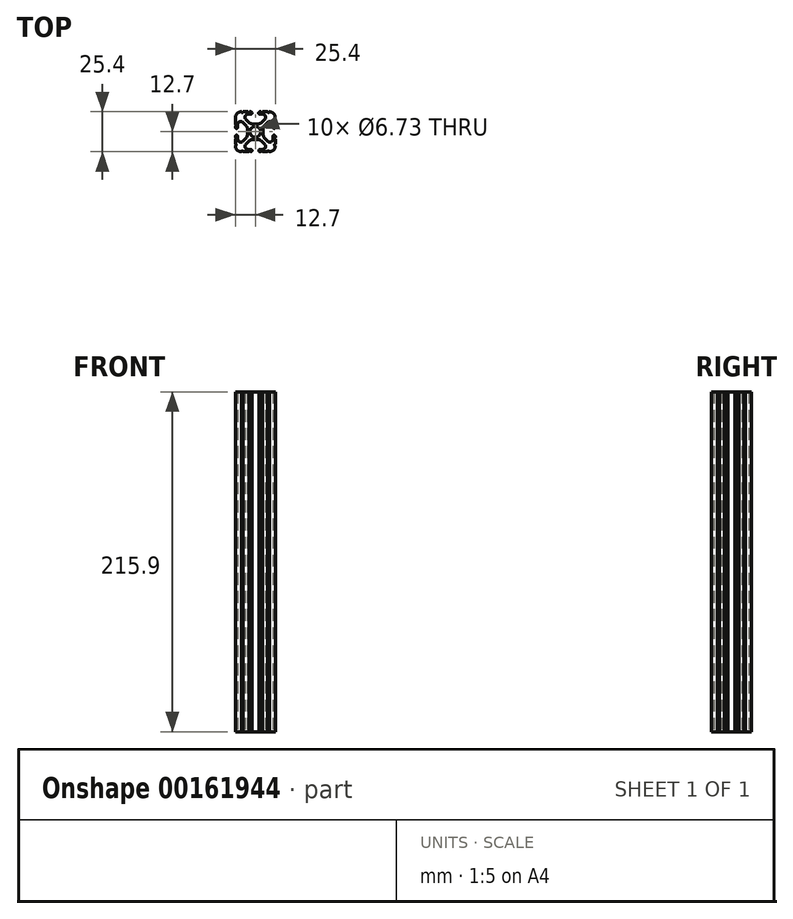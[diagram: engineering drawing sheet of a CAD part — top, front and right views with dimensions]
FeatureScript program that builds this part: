
annotation { "Feature Type Name" : "Feature", "Feature Type Description" : "" }
export const myFeature = defineFeature(function(context is Context, id is Id, definition is map)
    precondition{}
    {
        {
            var Q0;
            Q0=qCreatedBy(makeId("Top.planeOp"),FACE);
            var sketch = newSketch(context, id + "F0", { "sketchPlane" : qUnion([Q0])});
            skCircle(sketch, "E0", {"center": v(-12.7, 12.7) * mm, "radius": 3.36 * mm});
            skLineSegment(sketch, "E1.bottom", {"start": v(-11.24, 17.64) * mm, "end": v(-14.16, 17.64) * mm});
            skLineSegment(sketch, "E1.top", {"start": v(-11.24, 7.76) * mm, "end": v(-14.16, 7.76) * mm});
            skLineSegment(sketch, "E1.left", {"start": v(-7.76, 14.16) * mm, "end": v(-7.76, 11.24) * mm});
            skLineSegment(sketch, "E1.right", {"start": v(-17.64, 14.16) * mm, "end": v(-17.64, 11.24) * mm});
            skPoint(sketch, "E2.visualSharp", {"position": v(-25.4, 25.4) * mm});
            skPoint(sketch, "E3.visualSharp", {"position": v(0, 25.4) * mm});
            skPoint(sketch, "E4.visualSharp", {"position": v(0, 0) * mm});
            skPoint(sketch, "E5.visualSharp", {"position": v(-25.4, 0) * mm});
            skLineSegment(sketch, "E6.0", {"start": v(-18.7, 20.6) * mm, "end": v(-16.85, 18.76) * mm});
            skLineSegment(sketch, "E7.0", {"start": v(-20.6, 18.7) * mm, "end": v(-18.76, 16.85) * mm});
            skPoint(sketch, "E8.orphan", {"position": v(-23.85, 1.55) * mm});
            skPoint(sketch, "E9.orphan", {"position": v(-23.85, 23.85) * mm});
            skPoint(sketch, "E10.orphan", {"position": v(-1.55, 23.85) * mm});
            skPoint(sketch, "E11.orphan", {"position": v(-1.55, 1.55) * mm});
            skLineSegment(sketch, "E12", {"start": v(-8.55, 6.64) * mm, "end": v(-6.7, 4.8) * mm});
            skLineSegment(sketch, "E13.0", {"start": v(-18.7, 4.8) * mm, "end": v(-16.85, 6.64) * mm});
            skLineSegment(sketch, "E14.0", {"start": v(-20.6, 6.7) * mm, "end": v(-18.76, 8.55) * mm});
            skLineSegment(sketch, "E15.0", {"start": v(-8.55, 18.76) * mm, "end": v(-6.7, 20.6) * mm});
            skPoint(sketch, "E16.visualSharp", {"position": v(-23.85, 21.95) * mm});
            skArc(sketch, "E16.filletArc", {"start": v(-20.6, 18.7) * mm, "mid": v(-22.68, 19.1) * mm, "end": v(-23.85, 17.35) * mm});
            skPoint(sketch, "E17.visualSharp", {"position": v(-21.95, 23.85) * mm});
            skArc(sketch, "E17.filletArc", {"start": v(-17.35, 23.85) * mm, "mid": v(-19.1, 22.68) * mm, "end": v(-18.7, 20.6) * mm});
            skPoint(sketch, "E18.visualSharp", {"position": v(-5.34, 23.85) * mm});
            skLineSegment(sketch, "E19", {"start": v(-17.35, 23.85) * mm, "end": v(-15.58, 23.85) * mm});
            skLineSegment(sketch, "E20", {"start": v(-23.85, 17.35) * mm, "end": v(-23.85, 15.62) * mm});
            skLineSegment(sketch, "E21", {"start": v(-8.05, 1.55) * mm, "end": v(-9.78, 1.55) * mm});
            skArc(sketch, "E22.filletArc", {"start": v(-6.7, 20.6) * mm, "mid": v(-6.3, 22.68) * mm, "end": v(-8.05, 23.85) * mm});
            skPoint(sketch, "E23.visualSharp", {"position": v(-1.55, 3.45) * mm});
            skPoint(sketch, "E24.visualSharp", {"position": v(-3.45, 1.55) * mm});
            skArc(sketch, "E24.filletArc", {"start": v(-8.05, 1.55) * mm, "mid": v(-6.3, 2.73) * mm, "end": v(-6.7, 4.8) * mm});
            skArc(sketch, "E25.filletArc", {"start": v(-18.7, 4.8) * mm, "mid": v(-19.1, 2.73) * mm, "end": v(-17.35, 1.55) * mm});
            skArc(sketch, "E26.filletArc", {"start": v(-23.85, 8.05) * mm, "mid": v(-22.68, 6.3) * mm, "end": v(-20.6, 6.7) * mm});
            skLineSegment(sketch, "E27.bottom", {"start": v(-4.9, 0) * mm, "end": v(-8.05, 0) * mm});
            skLineSegment(sketch, "E27.top", {"start": v(-4.92, 25.4) * mm, "end": v(-8.05, 25.4) * mm});
            skLineSegment(sketch, "E27.left", {"start": v(0, 4.9) * mm, "end": v(0, 8.05) * mm});
            skLineSegment(sketch, "E27.right", {"start": v(-25.4, 4.9) * mm, "end": v(-25.4, 8.05) * mm});
            skArc(sketch, "E28.filletArc", {"start": v(-25.4, 3.81) * mm, "mid": v(-24.28, 1.12) * mm, "end": v(-21.59, 0) * mm});
            skArc(sketch, "E29.filletArc", {"start": v(-3.81, 0) * mm, "mid": v(-1.12, 1.12) * mm, "end": v(0, 3.8) * mm});
            skArc(sketch, "E30.filletArc", {"start": v(0, 21.59) * mm, "mid": v(-1.12, 24.28) * mm, "end": v(-3.8, 25.4) * mm});
            skArc(sketch, "E31.filletArc", {"start": v(-21.59, 25.4) * mm, "mid": v(-24.28, 24.28) * mm, "end": v(-25.4, 21.59) * mm});
            skPoint(sketch, "E32.newPointA", {"position": v(-17.64, 7.76) * mm});
            skArc(sketch, "E32.filletArc", {"start": v(-14.16, 7.76) * mm, "mid": v(-15.62, 7.47) * mm, "end": v(-16.85, 6.64) * mm});
            skPoint(sketch, "E33.newPointA", {"position": v(-7.76, 7.76) * mm});
            skArc(sketch, "E33.filletArc", {"start": v(-8.55, 6.64) * mm, "mid": v(-9.78, 7.47) * mm, "end": v(-11.24, 7.76) * mm});
            skArc(sketch, "E34.filletArc", {"start": v(-7.76, 11.24) * mm, "mid": v(-7.47, 9.78) * mm, "end": v(-6.64, 8.55) * mm});
            skArc(sketch, "E35.filletArc", {"start": v(-6.64, 16.85) * mm, "mid": v(-7.47, 15.62) * mm, "end": v(-7.76, 14.16) * mm});
            skPoint(sketch, "E36.newPointB", {"position": v(-7.76, 17.64) * mm});
            skArc(sketch, "E36.filletArc", {"start": v(-11.24, 17.64) * mm, "mid": v(-9.78, 17.93) * mm, "end": v(-8.55, 18.76) * mm});
            skPoint(sketch, "E37.newPointB", {"position": v(-17.64, 17.64) * mm});
            skArc(sketch, "E37.filletArc", {"start": v(-16.85, 18.76) * mm, "mid": v(-15.62, 17.93) * mm, "end": v(-14.16, 17.64) * mm});
            skArc(sketch, "E38.filletArc", {"start": v(-17.64, 14.16) * mm, "mid": v(-17.93, 15.62) * mm, "end": v(-18.76, 16.85) * mm});
            skArc(sketch, "E39.filletArc", {"start": v(-18.76, 8.55) * mm, "mid": v(-17.93, 9.78) * mm, "end": v(-17.64, 11.24) * mm});
            skLineSegment(sketch, "E40", {"start": v(-6.64, 8.55) * mm, "end": v(-4.8, 6.7) * mm});
            skPoint(sketch, "E41.visualSharp", {"position": v(-1.55, 21.95) * mm});
            skArc(sketch, "E42.filletArc", {"start": v(-4.8, 6.7) * mm, "mid": v(-2.73, 6.3) * mm, "end": v(-1.55, 8.05) * mm});
            skLineSegment(sketch, "E43", {"start": v(-1.55, 8.05) * mm, "end": v(-1.55, 9.78) * mm});
            skLineSegment(sketch, "E44", {"start": v(-6.64, 16.85) * mm, "end": v(-4.8, 18.7) * mm});
            skArc(sketch, "E45.filletArc", {"start": v(-1.55, 17.35) * mm, "mid": v(-2.73, 19.1) * mm, "end": v(-4.8, 18.7) * mm});
            skArc(sketch, "E46", {"start": v(-23.85, 9.78) * mm, "mid": v(-24.63, 10.56) * mm, "end": v(-25.4, 9.78) * mm});
            skArc(sketch, "E47", {"start": v(-25.4, 15.62) * mm, "mid": v(-24.63, 14.86) * mm, "end": v(-23.85, 15.62) * mm});
            skArc(sketch, "E48", {"start": v(-15.62, 23.85) * mm, "mid": v(-14.83, 24.63) * mm, "end": v(-15.62, 25.4) * mm});
            skArc(sketch, "E49", {"start": v(-9.78, 25.4) * mm, "mid": v(-10.6, 24.63) * mm, "end": v(-9.78, 23.85) * mm});
            skArc(sketch, "E50", {"start": v(-1.55, 15.62) * mm, "mid": v(-0.77, 14.88) * mm, "end": v(0, 15.62) * mm});
            skArc(sketch, "E51", {"start": v(0, 9.78) * mm, "mid": v(-0.77, 10.5) * mm, "end": v(-1.55, 9.78) * mm});
            skArc(sketch, "E52", {"start": v(-9.78, 1.55) * mm, "mid": v(-10.4, 0.77) * mm, "end": v(-9.78, 0) * mm});
            skArc(sketch, "E53", {"start": v(-15.62, 0) * mm, "mid": v(-14.85, 0.77) * mm, "end": v(-15.62, 1.55) * mm});
            skLineSegment(sketch, "E54.trimOffspring", {"start": v(-15.62, 1.55) * mm, "end": v(-17.35, 1.55) * mm});
            skLineSegment(sketch, "E55.trimOffspring", {"start": v(-16.7, 0) * mm, "end": v(-20.5, 0) * mm});
            skLineSegment(sketch, "E56.trimOffspring", {"start": v(-1.55, 15.62) * mm, "end": v(-1.55, 17.35) * mm});
            skLineSegment(sketch, "E57.trimOffspring", {"start": v(0, 15.62) * mm, "end": v(0, 16.26) * mm});
            skLineSegment(sketch, "E58.trimOffspring", {"start": v(-23.85, 9.78) * mm, "end": v(-23.85, 8.05) * mm});
            skLineSegment(sketch, "E59.trimOffspring", {"start": v(-25.4, 15.62) * mm, "end": v(-25.4, 16.26) * mm});
            skLineSegment(sketch, "E60.trimOffspring", {"start": v(-9.86, 23.85) * mm, "end": v(-8.05, 23.85) * mm});
            skLineSegment(sketch, "E61.trimOffspring", {"start": v(-15.58, 25.4) * mm, "end": v(-16.25, 25.4) * mm});
            skPoint(sketch, "E62.start.orphan", {"position": v(-15.62, 17.93) * mm});
            skPoint(sketch, "E63.start.orphan", {"position": v(-9.78, 17.93) * mm});
            skPoint(sketch, "E64.start.orphan", {"position": v(-7.47, 15.62) * mm});
            skPoint(sketch, "E65.start.orphan", {"position": v(-7.47, 9.78) * mm});
            skPoint(sketch, "E66.start.orphan", {"position": v(-17.93, 15.62) * mm});
            skPoint(sketch, "E67.start.orphan", {"position": v(-17.93, 9.78) * mm});
            skPoint(sketch, "E68.start.orphan", {"position": v(-9.78, 7.47) * mm});
            skPoint(sketch, "E69.start.orphan", {"position": v(-15.62, 7.47) * mm});
            skPoint(sketch, "E70.endSnap0", {"position": v(0, 18.6) * mm});
            skPoint(sketch, "E71.startSnap0", {"position": v(-1.55, 8.92) * mm});
            skArc(sketch, "E72", {"start": v(-4.92, 25.4) * mm, "mid": v(-4.37, 24.9) * mm, "end": v(-3.81, 25.4) * mm});
            skArc(sketch, "E73", {"start": v(-9.14, 25.4) * mm, "mid": v(-8.6, 24.86) * mm, "end": v(-8.05, 25.4) * mm});
            skArc(sketch, "E74", {"start": v(-17.35, 25.4) * mm, "mid": v(-16.8, 24.86) * mm, "end": v(-16.25, 25.4) * mm});
            skArc(sketch, "E75", {"start": v(-21.59, 25.4) * mm, "mid": v(-21.04, 24.85) * mm, "end": v(-20.49, 25.4) * mm});
            skLineSegment(sketch, "E76", {"start": v(-25.4, 21.59) * mm, "end": v(-25.4, 20.5) * mm});
            skArc(sketch, "E77", {"start": v(-25.4, 16.26) * mm, "mid": v(-24.84, 16.8) * mm, "end": v(-25.4, 17.35) * mm});
            skArc(sketch, "E78", {"start": v(-25.4, 8.05) * mm, "mid": v(-24.9, 8.6) * mm, "end": v(-25.4, 9.15) * mm});
            skArc(sketch, "E79", {"start": v(-25.4, 3.81) * mm, "mid": v(-24.85, 4.36) * mm, "end": v(-25.4, 4.9) * mm});
            skArc(sketch, "E80", {"start": v(-20.5, 0) * mm, "mid": v(-21.04, 0.55) * mm, "end": v(-21.59, 0) * mm});
            skArc(sketch, "E81", {"start": v(-15.62, 0) * mm, "mid": v(-16.16, 0.54) * mm, "end": v(-16.7, 0) * mm});
            skArc(sketch, "E82", {"start": v(-8.05, 0) * mm, "mid": v(-8.6, 0.55) * mm, "end": v(-9.15, 0) * mm});
            skArc(sketch, "E83", {"start": v(-3.81, 0) * mm, "mid": v(-4.35, 0.54) * mm, "end": v(-4.9, 0) * mm});
            skLineSegment(sketch, "E84.trimOffspring", {"start": v(-17.35, 25.4) * mm, "end": v(-20.49, 25.4) * mm});
            skLineSegment(sketch, "E85.trimOffspring", {"start": v(-25.4, 17.35) * mm, "end": v(-25.4, 21.59) * mm});
            skLineSegment(sketch, "E86.trimOffspring", {"start": v(-25.4, 9.15) * mm, "end": v(-25.4, 9.78) * mm});
            skLineSegment(sketch, "E87.trimOffspring", {"start": v(-9.15, 0) * mm, "end": v(-9.78, 0) * mm});
            skArc(sketch, "E88", {"start": v(0, 4.9) * mm, "mid": v(-0.54, 4.36) * mm, "end": v(0, 3.8) * mm});
            skArc(sketch, "E89", {"start": v(0, 9.15) * mm, "mid": v(-0.54, 8.6) * mm, "end": v(0, 8.05) * mm});
            skLineSegment(sketch, "E90.trimOffspring", {"start": v(0, 9.15) * mm, "end": v(0, 9.78) * mm});
            skArc(sketch, "E91", {"start": v(0, 21.59) * mm, "mid": v(-0.55, 21.04) * mm, "end": v(0, 20.5) * mm});
            skArc(sketch, "E92", {"start": v(0, 17.35) * mm, "mid": v(-0.55, 16.8) * mm, "end": v(0, 16.26) * mm});
            skLineSegment(sketch, "E93.trimOffspring", {"start": v(0, 17.35) * mm, "end": v(0, 20.5) * mm});
            skLineSegment(sketch, "E94.trimOffspring", {"start": v(-9.14, 25.4) * mm, "end": v(-9.86, 25.4) * mm});
            skSolve(sketch);
        }
        {
            var Q0;
            Q0=qSketchRegion(id+"F0",true);
            extrude(context, id + "F1", {"entities" : qUnion([Q0]), "depth" : 215.9 * mm});
        }
    });
